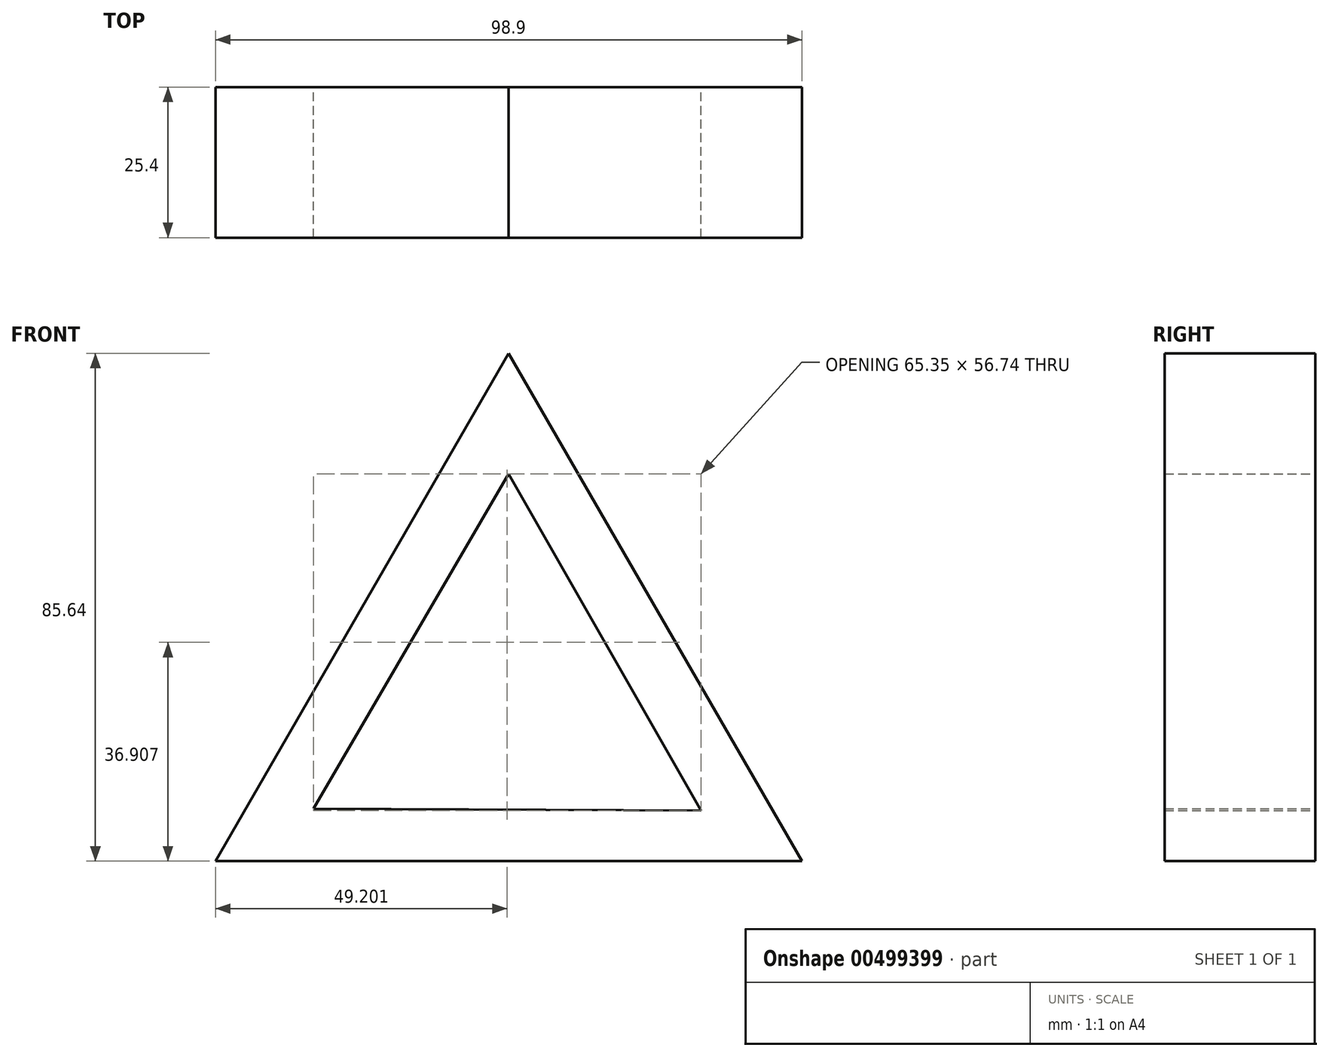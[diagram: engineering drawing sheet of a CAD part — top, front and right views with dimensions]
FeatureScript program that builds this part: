
annotation { "Feature Type Name" : "Feature", "Feature Type Description" : "" }
export const myFeature = defineFeature(function(context is Context, id is Id, definition is map)
    precondition{}
    {
        {
            var Q0;
            Q0=qCreatedBy(makeId("Front.planeOp"),FACE);
            var sketch = newSketch(context, id + "F0", { "sketchPlane" : qUnion([Q0])});
            skLineSegment(sketch, "E0", {"start": v(0, 0) * mm, "end": v(-49.45, -85.64) * mm});
            skLineSegment(sketch, "E1", {"start": v(-49.45, -85.64) * mm, "end": v(49.45, -85.64) * mm});
            skLineSegment(sketch, "E2", {"start": v(49.45, -85.64) * mm, "end": v(0, 0) * mm});
            skLineSegment(sketch, "E3", {"start": v(-32.92, -76.82) * mm, "end": v(0, -20.36) * mm});
            skLineSegment(sketch, "E4", {"start": v(0, -20.36) * mm, "end": v(32.43, -77.1) * mm});
            skLineSegment(sketch, "E5", {"start": v(32.43, -77.1) * mm, "end": v(-32.92, -76.82) * mm});
            skSolve(sketch);
        }
        {
            var Q0;
            Q0 = qSketchRegion(id + "F0", true);
            extrude(context, id + "F1", {"entities" : qUnion([Q0]), "depth" : 25.4 * mm});
        }
    });
